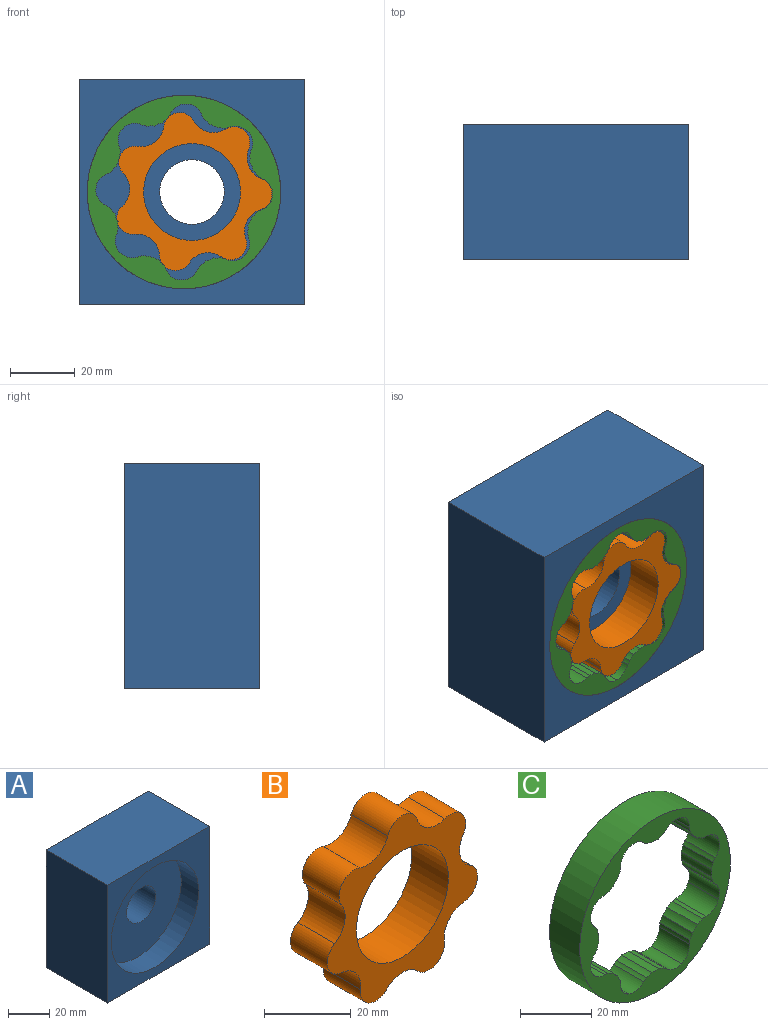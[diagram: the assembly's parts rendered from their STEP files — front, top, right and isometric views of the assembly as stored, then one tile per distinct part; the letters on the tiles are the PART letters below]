
ASSEMBLY  parts=3 mates=2
PART A: 9 faces, bbox 70x42x70 mm
  f0: plane 70x42mm, normal (0,0,1), area 2940mm2, adj f1,f3,f4,f6
  f1: plane 70x42mm, normal (-1,0,0), area 2940mm2, adj f0,f2,f4,f6
  f2: plane 70x42mm, normal (0,0,-1), area 2940mm2, adj f1,f3,f4,f6
  f3: plane 70x42mm, normal (1,0,0), area 2940mm2, adj f0,f2,f4,f6
  f4: plane 70x70mm, normal (0,1,0), area 4585.8mm2, adj f0,f1,f2,f3,f8
  f5: cylinder r=30mm len=60mm, axis (0,1,0), area 2261.9mm2, adj f6,f7
  f6: plane 70x70mm, normal (0,-1,0), area 2072.6mm2, adj f0,f1,f2,f3,f5
  f7: plane 60x60mm, normal (0,-1,0), area 2513.3mm2, adj f5,f8
  f8: cylinder r=10mm len=30mm, axis (0,-1,0), area 1885mm2, adj f4,f7
PART B: 17 faces, bbox 49x12x48 mm
  f0: cylinder r=7mm len=12mm, axis (0,1,0), area 135.8mm2, adj f1,f14,f15,f16
  f1: cylinder r=5mm len=12mm, axis (0,1,0), area 150.9mm2, adj f0,f2,f15,f16
  f2: cylinder r=7mm len=12mm, axis (0,1,0), area 135.8mm2, adj f1,f3,f15,f16
  f3: cylinder r=5mm len=12mm, axis (0,1,0), area 150.9mm2, adj f2,f4,f15,f16
  f4: cylinder r=7mm len=12mm, axis (0,1,0), area 135.8mm2, adj f3,f5,f15,f16
  f5: cylinder r=5mm len=12mm, axis (0,1,0), area 150.9mm2, adj f4,f6,f15,f16
  f6: cylinder r=7mm len=12mm, axis (0,1,0), area 135.8mm2, adj f5,f7,f15,f16
  f7: cylinder r=5mm len=12mm, axis (0,1,0), area 150.9mm2, adj f6,f8,f15,f16
  f8: cylinder r=7mm len=12mm, axis (0,1,0), area 135.8mm2, adj f7,f9,f15,f16
  f9: cylinder r=5mm len=12mm, axis (0,1,0), area 150.9mm2, adj f8,f10,f15,f16
  f10: cylinder r=7mm len=12mm, axis (0,1,0), area 135.8mm2, adj f9,f11,f15,f16
  f11: cylinder r=5mm len=12mm, axis (0,1,0), area 150.9mm2, adj f10,f12,f15,f16
  f12: cylinder r=7mm len=12mm, axis (0,1,0), area 135.8mm2, adj f11,f14,f15,f16
  f13: cylinder r=15mm len=30mm, axis (0,1,0), area 1131mm2, adj f15,f16
  f14: cylinder r=5mm len=12mm, axis (0,1,0), area 150.9mm2, adj f0,f12,f15,f16
  f15: plane 49x48.02mm, normal (0,-1,0), area 833.9mm2, adj f0,f1,f2,f3,f4,f5,f6,f7
  f16: plane 49x48.02mm, normal (0,1,0), area 833.9mm2, adj f0,f1,f2,f3,f4,f5,f6,f7
PART C: 59 faces, bbox 60x12x60 mm
  f0: cylinder r=5mm len=12mm, axis (0,-1,0), area 16.7mm2, adj f1,f55,f57,f58
  f1: cylinder r=5mm len=12mm, axis (0,-1,0), area 27.4mm2, adj f0,f2,f57,f58
  f2: cylinder r=5mm len=12mm, axis (0,-1,0), area 32mm2, adj f1,f3,f57,f58
  f3: cylinder r=5mm len=12mm, axis (0,-1,0), area 27.4mm2, adj f2,f4,f57,f58
  f4: cylinder r=5mm len=12mm, axis (0,-1,0), area 16.7mm2, adj f3,f5,f57,f58
  f5: cylinder r=5mm len=12mm, axis (0,-1,0), area 77.3mm2, adj f4,f6,f57,f58
  f6: cylinder r=5mm len=12mm, axis (0,-1,0), area 77.3mm2, adj f5,f7,f57,f58
  f7: cylinder r=5mm len=12mm, axis (0,-1,0), area 16.7mm2, adj f6,f8,f57,f58
  f8: cylinder r=5mm len=12mm, axis (0,-1,0), area 27.4mm2, adj f7,f9,f57,f58
  f9: cylinder r=5mm len=12mm, axis (0,-1,0), area 32mm2, adj f8,f10,f57,f58
  f10: cylinder r=5mm len=12mm, axis (0,-1,0), area 27.4mm2, adj f9,f11,f57,f58
  f11: cylinder r=5mm len=12mm, axis (0,-1,0), area 16.7mm2, adj f10,f12,f57,f58
  f12: cylinder r=5mm len=12mm, axis (0,-1,0), area 77.3mm2, adj f11,f13,f57,f58
  f13: cylinder r=5mm len=12mm, axis (0,-1,0), area 77.3mm2, adj f12,f14,f57,f58
  f14: cylinder r=5mm len=12mm, axis (0,-1,0), area 16.7mm2, adj f13,f15,f57,f58
  f15: cylinder r=5mm len=12mm, axis (0,-1,0), area 27.4mm2, adj f14,f16,f57,f58
  f16: cylinder r=5mm len=12mm, axis (0,-1,0), area 32mm2, adj f15,f17,f57,f58
  f17: cylinder r=5mm len=12mm, axis (0,-1,0), area 27.4mm2, adj f16,f18,f57,f58
  f18: cylinder r=5mm len=12mm, axis (0,-1,0), area 16.7mm2, adj f17,f19,f57,f58
  f19: cylinder r=5mm len=12mm, axis (0,-1,0), area 77.3mm2, adj f18,f20,f57,f58
  f20: cylinder r=5mm len=12mm, axis (0,-1,0), area 77.3mm2, adj f19,f21,f57,f58
  f21: cylinder r=5mm len=12mm, axis (0,-1,0), area 16.7mm2, adj f20,f22,f57,f58
  f22: cylinder r=5mm len=12mm, axis (0,-1,0), area 27.4mm2, adj f21,f23,f57,f58
  f23: cylinder r=5mm len=12mm, axis (0,-1,0), area 32mm2, adj f22,f24,f57,f58
  f24: cylinder r=5mm len=12mm, axis (0,-1,0), area 27.4mm2, adj f23,f25,f57,f58
  f25: cylinder r=5mm len=12mm, axis (0,-1,0), area 16.7mm2, adj f24,f26,f57,f58
  f26: cylinder r=5mm len=12mm, axis (0,-1,0), area 77.3mm2, adj f25,f27,f57,f58
  f27: cylinder r=5mm len=12mm, axis (0,-1,0), area 77.3mm2, adj f26,f28,f57,f58
  f28: cylinder r=5mm len=12mm, axis (0,-1,0), area 16.7mm2, adj f27,f29,f57,f58
  f29: cylinder r=5mm len=12mm, axis (0,-1,0), area 27.4mm2, adj f28,f30,f57,f58
  f30: cylinder r=5mm len=12mm, axis (0,-1,0), area 32mm2, adj f29,f31,f57,f58
  f31: cylinder r=5mm len=12mm, axis (0,-1,0), area 27.4mm2, adj f30,f32,f57,f58
  f32: cylinder r=5mm len=12mm, axis (0,-1,0), area 16.7mm2, adj f31,f33,f57,f58
  f33: cylinder r=5mm len=12mm, axis (0,-1,0), area 77.3mm2, adj f32,f34,f57,f58
  f34: cylinder r=5mm len=12mm, axis (0,-1,0), area 77.3mm2, adj f33,f35,f57,f58
  f35: cylinder r=5mm len=12mm, axis (0,-1,0), area 16.7mm2, adj f34,f36,f57,f58
  f36: cylinder r=5mm len=12mm, axis (0,-1,0), area 27.4mm2, adj f35,f37,f57,f58
  f37: cylinder r=5mm len=12mm, axis (0,-1,0), area 32mm2, adj f36,f38,f57,f58
  f38: cylinder r=5mm len=12mm, axis (0,-1,0), area 27.4mm2, adj f37,f39,f57,f58
  f39: cylinder r=5mm len=12mm, axis (0,-1,0), area 16.7mm2, adj f38,f40,f57,f58
  f40: cylinder r=5mm len=12mm, axis (0,-1,0), area 77.3mm2, adj f39,f41,f57,f58
  f41: cylinder r=5mm len=12mm, axis (0,-1,0), area 77.3mm2, adj f40,f42,f57,f58
  f42: cylinder r=5mm len=12mm, axis (0,-1,0), area 16.7mm2, adj f41,f43,f57,f58
  f43: cylinder r=5mm len=12mm, axis (0,-1,0), area 27.4mm2, adj f42,f44,f57,f58
  f44: cylinder r=5mm len=12mm, axis (0,-1,0), area 32mm2, adj f43,f45,f57,f58
  f45: cylinder r=5mm len=12mm, axis (0,-1,0), area 27.4mm2, adj f44,f46,f57,f58
  f46: cylinder r=5mm len=12mm, axis (0,-1,0), area 16.7mm2, adj f45,f47,f57,f58
  f47: cylinder r=5mm len=12mm, axis (0,-1,0), area 77.3mm2, adj f46,f48,f57,f58
  f48: cylinder r=5mm len=12mm, axis (0,-1,0), area 77.3mm2, adj f47,f49,f57,f58
  f49: cylinder r=5mm len=12mm, axis (0,-1,0), area 16.7mm2, adj f48,f50,f57,f58
  f50: cylinder r=5mm len=12mm, axis (0,-1,0), area 27.4mm2, adj f49,f51,f57,f58
  f51: cylinder r=5mm len=12mm, axis (0,-1,0), area 32mm2, adj f50,f52,f57,f58
  f52: cylinder r=5mm len=12mm, axis (0,-1,0), area 27.4mm2, adj f51,f53,f57,f58
  f53: cylinder r=5mm len=12mm, axis (0,-1,0), area 16.7mm2, adj f52,f54,f57,f58
  f54: cylinder r=5mm len=12mm, axis (0,-1,0), area 77.3mm2, adj f53,f55,f57,f58
  f55: cylinder r=5mm len=12mm, axis (0,-1,0), area 77.3mm2, adj f0,f54,f57,f58
  f56: cylinder r=30mm len=60mm, axis (0,-1,0), area 2261.9mm2, adj f57,f58
  f57: plane 60x60mm, normal (0,1,0), area 889.2mm2, adj f0,f1,f2,f3,f4,f5,f6,f7
  f58: plane 60x60mm, normal (0,-1,0), area 889.2mm2, adj f0,f1,f2,f3,f4,f5,f6,f7
PLACE A t=(-5.73,37.76,1.41)mm fixed
PLACE B rot(axis=(0,1,0),143.3deg) t=(-5.73,-4.24,1.41)mm
PLACE C rot(axis=(0,-1,0),110.9deg) t=(-5.9,-4.24,2.3)mm
MATE revolute B.f13 <-> A.f8  axis (0,1,0) through (-5.73,-4.24,1.41)mm
MATE revolute C.f56 <-> A.f5  axis (0,1,0) through (-8.23,-4.24,1.41)mm
